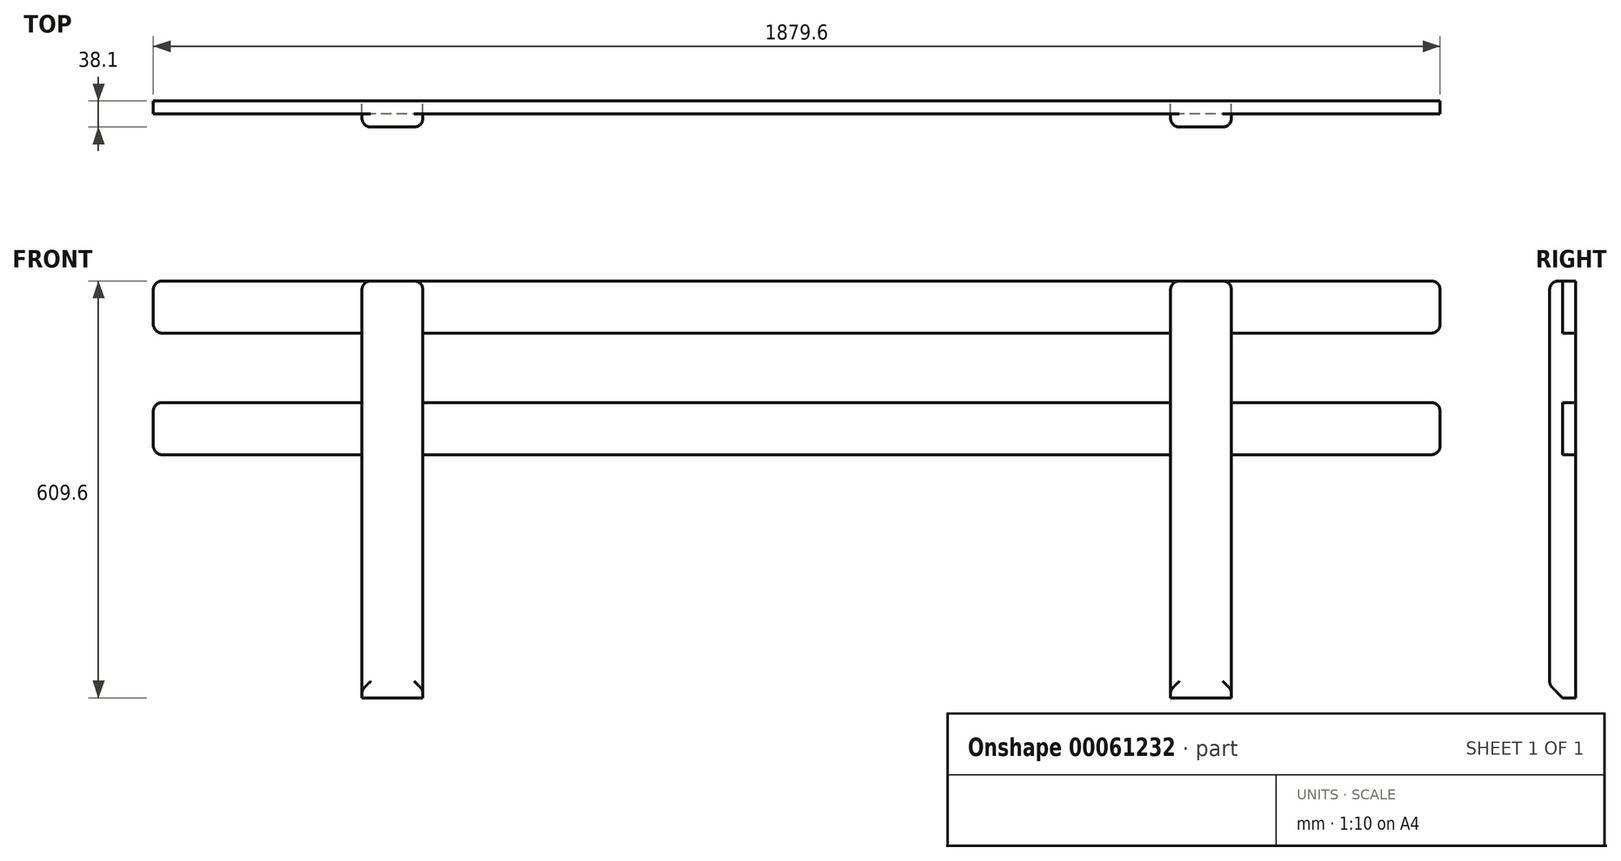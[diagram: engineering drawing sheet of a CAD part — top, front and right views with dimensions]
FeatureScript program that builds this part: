
annotation { "Feature Type Name" : "Feature", "Feature Type Description" : "" }
export const myFeature = defineFeature(function(context is Context, id is Id, definition is map)
    precondition{}
    {
        {
            var Q0;
            Q0=qCreatedBy(makeId("Right.planeOp"),FACE);
            var sketch = newSketch(context, id + "F0", { "sketchPlane" : qUnion([Q0])});
            skLineSegment(sketch, "E0.bottom", {"start": v(0, 457.2) * mm, "end": v(-19.05, 457.2) * mm, "construction": true});
            skLineSegment(sketch, "E0.top", {"start": v(0, 381) * mm, "end": v(-19.05, 381) * mm, "construction": true});
            skLineSegment(sketch, "E0.left", {"start": v(0, 457.2) * mm, "end": v(0, 381) * mm, "construction": true});
            skLineSegment(sketch, "E0.right", {"start": v(-19.05, 457.2) * mm, "end": v(-19.05, 381) * mm, "construction": true});
            skLineSegment(sketch, "E1.bottom", {"start": v(0, 533.4) * mm, "end": v(-19.05, 533.4) * mm});
            skLineSegment(sketch, "E1.top", {"start": v(0, 609.6) * mm, "end": v(-19.05, 609.6) * mm});
            skLineSegment(sketch, "E1.left", {"start": v(0, 533.4) * mm, "end": v(0, 609.6) * mm});
            skLineSegment(sketch, "E1.right", {"start": v(-19.05, 533.4) * mm, "end": v(-19.05, 609.6) * mm});
            skSolve(sketch);
        }
        {
            var Q0;
            Q0 = qSketchRegion(id + "F0", true);
            extrude(context, id + "F1", {"entities" : qUnion([Q0]), "depth" : 1879.6 * mm, "symmetric" : true});
        }
        {
            var Q0;
            Q0=makeQuery(id+"F1.opExtrude","SWEPT_FACE",FACE,{"disambiguationData":[OSD([sQuery(id+"F0.wireOp",EDGE,"E1.top")])]});
            var sketch = newSketch(context, id + "F2", { "sketchPlane" : qUnion([Q0])});
            skLineSegment(sketch, "E2.bottom", {"start": v(635, 0) * mm, "end": v(546.1, 0) * mm});
            skLineSegment(sketch, "E2.top", {"start": v(635, -38.1) * mm, "end": v(546.1, -38.1) * mm});
            skLineSegment(sketch, "E2.left", {"start": v(635, 0) * mm, "end": v(635, -38.1) * mm});
            skLineSegment(sketch, "E2.right", {"start": v(546.1, 0) * mm, "end": v(546.1, -38.1) * mm});
            skLineSegment(sketch, "E3.bottom", {"start": v(-635, 0) * mm, "end": v(-546.1, 0) * mm});
            skLineSegment(sketch, "E3.top", {"start": v(-635, -38.1) * mm, "end": v(-546.1, -38.1) * mm});
            skLineSegment(sketch, "E3.left", {"start": v(-635, 0) * mm, "end": v(-635, -38.1) * mm});
            skLineSegment(sketch, "E3.right", {"start": v(-546.1, 0) * mm, "end": v(-546.1, -38.1) * mm});
            skSolve(sketch);
        }
        {
            var Q0;
            Q0 = qSketchRegion(id + "F2", true);
            var Q1;
            Q1=qCreatedBy(makeId("Top.planeOp"),FACE);
            extrude(context, id + "F3", {"entities" : qUnion([Q0]), "operationType" : NewBodyOperationType.ADD, "endBound" : BoundingType.UP_TO_SURFACE, "oppositeDirection" : true, "endBoundEntityFace" : qUnion([Q1]), "depth" : 25.4 * mm});
        }
        {
            var Q0;
            Q0=makeQuery(id+"F3.opExtrude","CAP_EDGE",EDGE,{"disambiguationData":[OSD([sQuery(id+"F2.wireOp",EDGE,"E2.top")])],"isStart":false});
            var Q1;
            Q1=makeQuery(id+"F3.opExtrude","CAP_EDGE",EDGE,{"disambiguationData":[OSD([sQuery(id+"F2.wireOp",EDGE,"E3.top")])],"isStart":false});
            chamfer(context, id + "F4", {"entities" : qUnion([Q0, Q1]), "width" : 19.05 * mm, "tangentPropagation" : true});
        }
        {
            var Q0;
            Q0=qCreatedBy(makeId("Right.planeOp"),FACE);
            var sketch = newSketch(context, id + "F5", { "sketchPlane" : qUnion([Q0])});
            skLineSegment(sketch, "E4.bottom", {"start": v(0, 431.8) * mm, "end": v(-19.05, 431.8) * mm});
            skLineSegment(sketch, "E4.top", {"start": v(0, 355.6) * mm, "end": v(-19.05, 355.6) * mm});
            skLineSegment(sketch, "E4.left", {"start": v(0, 431.8) * mm, "end": v(0, 355.6) * mm});
            skLineSegment(sketch, "E4.right", {"start": v(-19.05, 431.8) * mm, "end": v(-19.05, 355.6) * mm});
            skSolve(sketch);
        }
        {
            var Q0;
            Q0 = qSketchRegion(id + "F5", true);
            extrude(context, id + "F6", {"entities" : qUnion([Q0]), "operationType" : NewBodyOperationType.ADD, "depth" : 1879.6 * mm, "symmetric" : true});
        }
        {
            var Q0;
            Q0=makeQuery(id+"F1.opExtrude","CAP_EDGE",EDGE,{"disambiguationData":[OSD([sQuery(id+"F0.wireOp",EDGE,"E1.top")])],"isStart":false});
            var Q1;
            Q1=makeQuery(id+"F1.opExtrude","CAP_EDGE",EDGE,{"disambiguationData":[OSD([sQuery(id+"F0.wireOp",EDGE,"E1.bottom")])],"isStart":false});
            var Q2;
            Q2=makeQuery(id+"F1.opExtrude","CAP_EDGE",EDGE,{"disambiguationData":[OSD([sQuery(id+"F0.wireOp",EDGE,"E0.bottom")])],"isStart":false});
            var Q3;
            Q3=makeQuery(id+"F1.opExtrude","CAP_EDGE",EDGE,{"disambiguationData":[OSD([sQuery(id+"F0.wireOp",EDGE,"E0.top")])],"isStart":false});
            var Q4;
            Q4=makeQuery(id+"F3.opExtrude","CAP_EDGE",EDGE,{"disambiguationData":[OSD([sQuery(id+"F2.wireOp",EDGE,"E2.top")])],"isStart":true});
            var Q5;
            Q5=makeQuery(id+"F3.opExtrude","CAP_EDGE",EDGE,{"disambiguationData":[OSD([sQuery(id+"F2.wireOp",EDGE,"E2.left")])],"isStart":true});
            var Q6;
            Q6=makeQuery(id+"F3.opExtrude","CAP_EDGE",EDGE,{"disambiguationData":[OSD([sQuery(id+"F2.wireOp",EDGE,"E2.right")])],"isStart":true});
            var Q7;
            Q7=makeQuery(id+"F3.opExtrude","SWEPT_EDGE",EDGE,{"disambiguationData":[OSD([sQuery(id+"F2.wireOp",EDGE,"E2.top"),sQuery(id+"F2.wireOp",EDGE,"E2.left")])]});
            var Q8;
            Q8=makeQuery(id+"F3.opExtrude","SWEPT_EDGE",EDGE,{"disambiguationData":[OSD([sQuery(id+"F2.wireOp",EDGE,"E2.top"),sQuery(id+"F2.wireOp",EDGE,"E2.right")])]});
            var Q9;
            Q9=makeQuery(id+"F3.opExtrude","CAP_EDGE",EDGE,{"disambiguationData":[OSD([sQuery(id+"F2.wireOp",EDGE,"E3.top")])],"isStart":true});
            var Q10;
            Q10=makeQuery(id+"F3.opExtrude","SWEPT_EDGE",EDGE,{"disambiguationData":[OSD([sQuery(id+"F2.wireOp",EDGE,"E3.top"),sQuery(id+"F2.wireOp",EDGE,"E3.right")])]});
            var Q11;
            Q11=makeQuery(id+"F3.opExtrude","SWEPT_EDGE",EDGE,{"disambiguationData":[OSD([sQuery(id+"F2.wireOp",EDGE,"E3.top"),sQuery(id+"F2.wireOp",EDGE,"E3.left")])]});
            var Q12;
            Q12=makeQuery(id+"F3.opExtrude","CAP_EDGE",EDGE,{"disambiguationData":[OSD([sQuery(id+"F2.wireOp",EDGE,"E3.left")])],"isStart":true});
            var Q13;
            Q13=makeQuery(id+"F1.opExtrude","CAP_EDGE",EDGE,{"disambiguationData":[OSD([sQuery(id+"F0.wireOp",EDGE,"E1.top")])],"isStart":true});
            var Q14;
            Q14=makeQuery(id+"F1.opExtrude","CAP_EDGE",EDGE,{"disambiguationData":[OSD([sQuery(id+"F0.wireOp",EDGE,"E1.bottom")])],"isStart":true});
            var Q15;
            Q15=makeQuery(id+"F1.opExtrude","CAP_EDGE",EDGE,{"disambiguationData":[OSD([sQuery(id+"F0.wireOp",EDGE,"E0.bottom")])],"isStart":true});
            var Q16;
            Q16=makeQuery(id+"F1.opExtrude","CAP_EDGE",EDGE,{"disambiguationData":[OSD([sQuery(id+"F0.wireOp",EDGE,"E0.top")])],"isStart":true});
            var Q17;
            Q17=makeQuery(id+"F3.opExtrude","CAP_EDGE",EDGE,{"disambiguationData":[OSD([sQuery(id+"F2.wireOp",EDGE,"E3.right")])],"isStart":true});
            var Q18;
            {var subQ0=sQuery(id+"F2.wireOp",EDGE,"E3.top");Q18=makeQuery(id+"F4.opChamfer","BLEND_EDGE",EDGE,{"blendedFrom":[makeQuery(id+"F3.opExtrude","CAP_EDGE",EDGE,{"disambiguationData":[OSD([subQ0])],"isStart":false}),makeQuery(id+"F3.opExtrude","SWEPT_FACE",FACE,{"disambiguationData":[OSD([subQ0])]})],"blendedInto":[makeQuery(id+"F3.opExtrude","SWEPT_FACE",FACE,{"disambiguationData":[OSD([subQ0])]})]});}
            var Q19;
            {var subQ0=sQuery(id+"F2.wireOp",EDGE,"E2.top");Q19=makeQuery(id+"F4.opChamfer","BLEND_EDGE",EDGE,{"blendedFrom":[makeQuery(id+"F3.opExtrude","CAP_EDGE",EDGE,{"disambiguationData":[OSD([subQ0])],"isStart":false}),makeQuery(id+"F3.opExtrude","SWEPT_FACE",FACE,{"disambiguationData":[OSD([subQ0])]})],"blendedInto":[makeQuery(id+"F3.opExtrude","SWEPT_FACE",FACE,{"disambiguationData":[OSD([subQ0])]})]});}
            var Q20;
            Q20=makeQuery(id+"F6.opExtrude","CAP_EDGE",EDGE,{"disambiguationData":[OSD([sQuery(id+"F5.wireOp",EDGE,"E4.bottom")])],"isStart":false});
            var Q21;
            Q21=makeQuery(id+"F6.opExtrude","CAP_EDGE",EDGE,{"disambiguationData":[OSD([sQuery(id+"F5.wireOp",EDGE,"E4.top")])],"isStart":false});
            var Q22;
            Q22=makeQuery(id+"F6.opExtrude","CAP_EDGE",EDGE,{"disambiguationData":[OSD([sQuery(id+"F5.wireOp",EDGE,"E4.bottom")])],"isStart":true});
            var Q23;
            Q23=makeQuery(id+"F6.opExtrude","CAP_EDGE",EDGE,{"disambiguationData":[OSD([sQuery(id+"F5.wireOp",EDGE,"E4.top")])],"isStart":true});
            fillet(context, id + "F7", {"entities" : qUnion([Q0, Q1, Q2, Q3, Q4, Q5, Q6, Q7, Q8, Q9, Q10, Q11, Q12, Q13, Q14, Q15, Q16, Q17, Q18, Q19, Q20, Q21, Q22, Q23]), "radius" : 12.7 * mm, "tangentPropagation" : true, "allowEdgeOverflow" : false});
        }
    });
